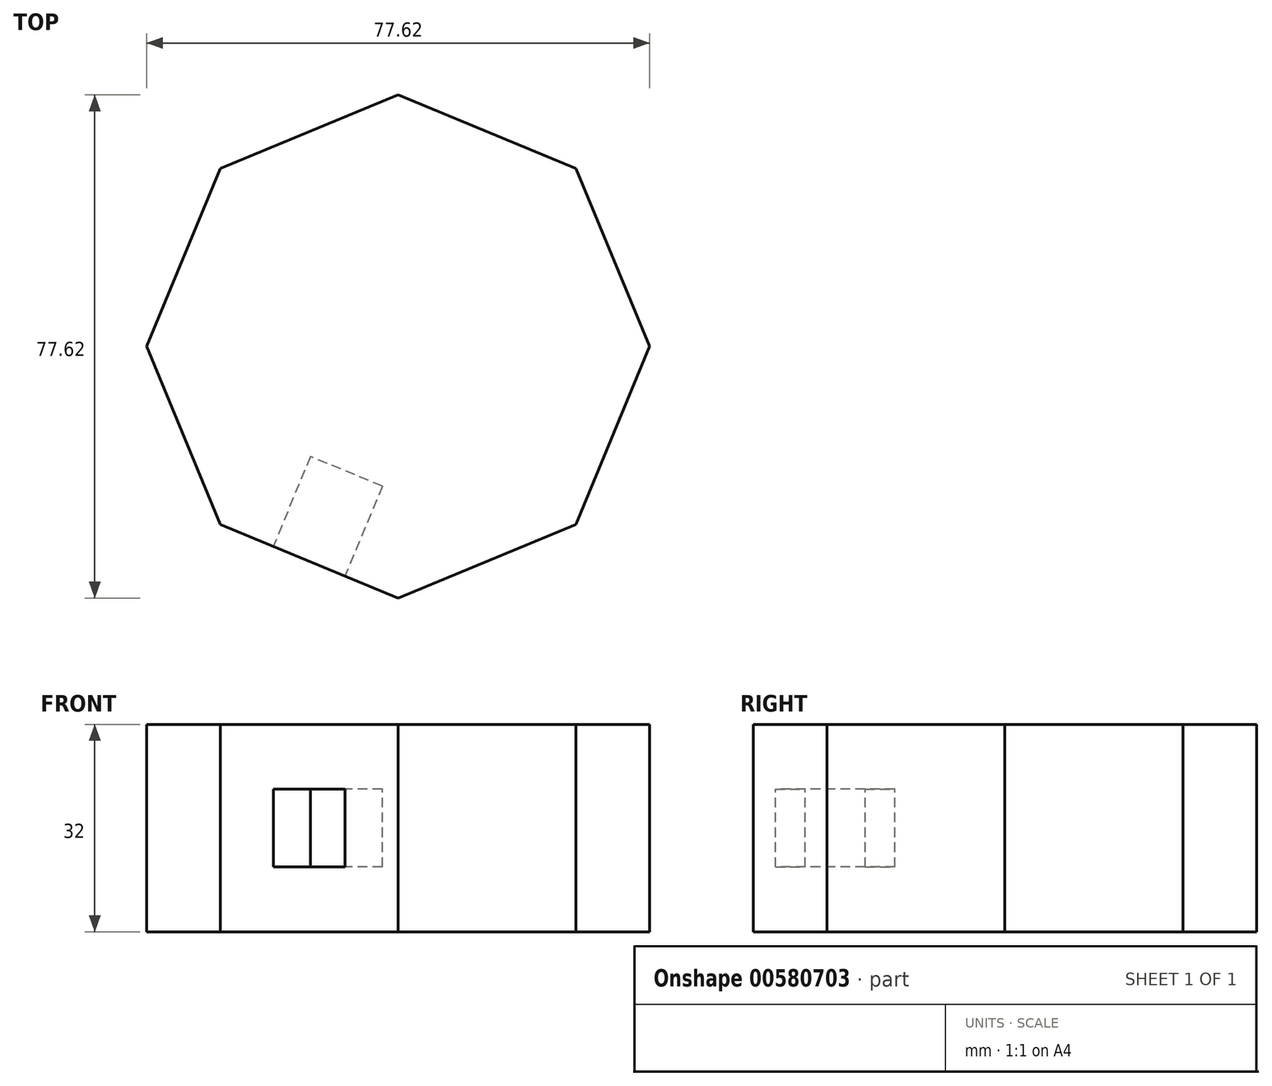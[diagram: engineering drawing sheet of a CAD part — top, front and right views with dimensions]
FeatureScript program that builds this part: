
annotation { "Feature Type Name" : "Feature", "Feature Type Description" : "" }
export const myFeature = defineFeature(function(context is Context, id is Id, definition is map)
    precondition{}
    {
        {
            var Q0;
            Q0=qCreatedBy(makeId("Top.planeOp"),FACE);
            var sketch = newSketch(context, id + "F0", { "sketchPlane" : qUnion([Q0])});
            skCircle(sketch, "E0.cCircle", {"center": v(0, 0) * mm, "radius": 38.81 * mm, "construction": true});
            skLineSegment(sketch, "E0.0", {"start": v(-38.81, 0) * mm, "end": v(-27.45, 27.45) * mm});
            skLineSegment(sketch, "E0.1", {"start": v(-27.45, 27.45) * mm, "end": v(0, 38.81) * mm});
            skLineSegment(sketch, "E0.2", {"start": v(0, 38.81) * mm, "end": v(27.45, 27.45) * mm});
            skLineSegment(sketch, "E0.3", {"start": v(27.45, 27.45) * mm, "end": v(38.81, 0) * mm});
            skLineSegment(sketch, "E0.4", {"start": v(38.81, 0) * mm, "end": v(27.45, -27.45) * mm});
            skLineSegment(sketch, "E0.5", {"start": v(27.45, -27.45) * mm, "end": v(0, -38.81) * mm});
            skLineSegment(sketch, "E0.6", {"start": v(0, -38.81) * mm, "end": v(-27.45, -27.45) * mm});
            skLineSegment(sketch, "E0.7", {"start": v(-27.45, -27.45) * mm, "end": v(-38.81, 0) * mm});
            skSolve(sketch);
        }
        {
            var Q0;
            Q0=makeQuery(id+"F0.imprint","IMPRINT",FACE,{"disambiguationData":[TD([[makeQuery(id+"F0.imprint","IMPRINT",EDGE,{"derivedFrom":sQuery(id+"F0.wireOp",EDGE,"E0.0")}),-1.0]])]});
            extrude(context, id + "F1", {"entities" : qUnion([Q0]), "endBound" : BoundingType.SYMMETRIC, "depth" : 32 * mm, "offsetDistance" : 25 * mm});
        }
        {
            var Q0;
            Q0=makeQuery(id+"F1.opExtrude","SWEPT_FACE",FACE,{"disambiguationData":[OSD([sQuery(id+"F0.wireOp",EDGE,"E0.6")])]});
            var sketch = newSketch(context, id + "F2", { "sketchPlane" : qUnion([Q0])});
            skLineSegment(sketch, "E1.bottom", {"start": v(6, -6) * mm, "end": v(-6, -6) * mm});
            skLineSegment(sketch, "E1.top", {"start": v(6, 6) * mm, "end": v(-6, 6) * mm});
            skLineSegment(sketch, "E1.left", {"start": v(6, -6) * mm, "end": v(6, 6) * mm});
            skLineSegment(sketch, "E1.right", {"start": v(-6, -6) * mm, "end": v(-6, 6) * mm});
            skPoint(sketch, "E1.middle", {"position": v(0, 0) * mm});
            skSolve(sketch);
        }
        {
            var Q0;
            Q0=qCreatedBy(makeId("Front.planeOp"),FACE);
            var sketch = newSketch(context, id + "F3", { "sketchPlane" : qUnion([Q0])});
            skLineSegment(sketch, "E2", {"start": v(0, 65.95) * mm, "end": v(0, -70.04) * mm});
            skSolve(sketch);
        }
        {
            var Q0;
            Q0=makeQuery(id+"F2.imprint","IMPRINT",FACE,{"disambiguationData":[TD([[makeQuery(id+"F2.imprint","IMPRINT",EDGE,{"derivedFrom":sQuery(id+"F2.wireOp",EDGE,"E1.bottom")}),-1.0]])]});
            extrude(context, id + "F4", {"entities" : qUnion([Q0]), "operationType" : NewBodyOperationType.REMOVE, "oppositeDirection" : true, "depth" : 15 * mm, "offsetDistance" : 25 * mm});
        }
        {
            var Q0;
            Q0=qCreatedBy(makeId("Top.planeOp"),FACE);
            var sketch = newSketch(context, id + "F5", { "sketchPlane" : qUnion([Q0])});
            skLineSegment(sketch, "E3.bottom", {"start": v(16, -16) * mm, "end": v(-16, -16) * mm});
            skLineSegment(sketch, "E3.top", {"start": v(16, 16) * mm, "end": v(-16, 16) * mm});
            skLineSegment(sketch, "E3.left", {"start": v(16, -16) * mm, "end": v(16, 16) * mm});
            skLineSegment(sketch, "E3.right", {"start": v(-16, -16) * mm, "end": v(-16, 16) * mm});
            skPoint(sketch, "E3.middle", {"position": v(0, 0) * mm});
            skSolve(sketch);
        }
        {
            var Q0;
            Q0=makeQuery(id+"F5.imprint","IMPRINT",FACE,{"disambiguationData":[TD([[makeQuery(id+"F5.imprint","IMPRINT",EDGE,{"derivedFrom":sQuery(id+"F5.wireOp",EDGE,"E3.bottom")}),-1.0]])]});
            extrude(context, id + "F6", {"entities" : qUnion([Q0]), "endBound" : BoundingType.SYMMETRIC, "depth" : 77.25 * mm, "offsetDistance" : 25 * mm});
        }
        {
            var Q0;
            Q0=makeQuery(id+"F6.opExtrude","SWEPT_BODY",BODY,{"disambiguationData":[OSD([sQuery(id+"F5.wireOp",EDGE,"E3.bottom"),sQuery(id+"F5.wireOp",EDGE,"E3.top"),sQuery(id+"F5.wireOp",EDGE,"E3.left"),sQuery(id+"F5.wireOp",EDGE,"E3.right")])]});
            deleteBodies(context, id + "F7", {"entities" : qUnion([Q0])});
        }
    });
